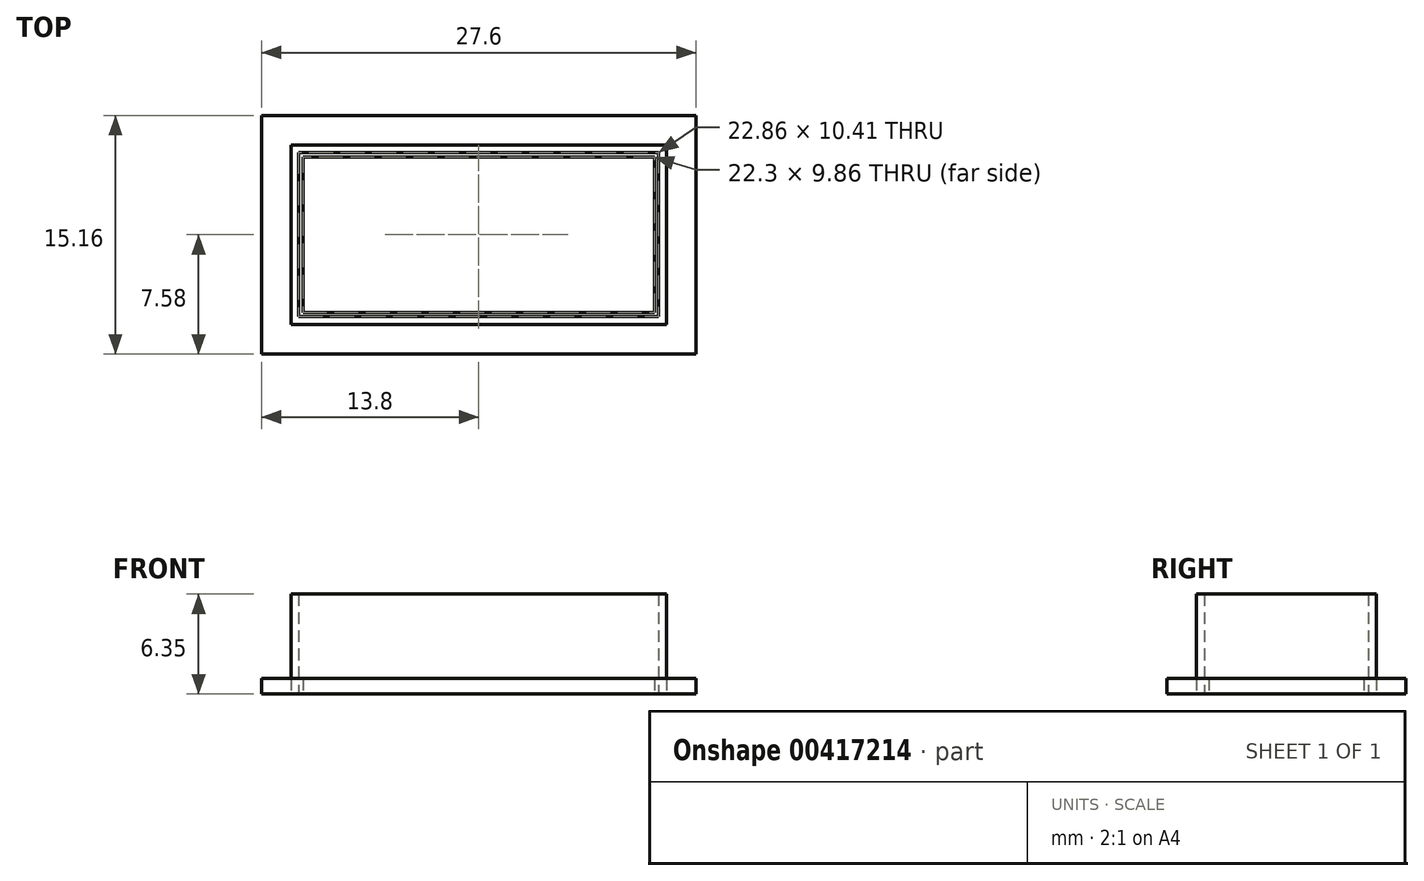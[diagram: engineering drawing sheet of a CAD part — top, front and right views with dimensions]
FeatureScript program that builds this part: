
annotation { "Feature Type Name" : "Feature", "Feature Type Description" : "" }
export const myFeature = defineFeature(function(context is Context, id is Id, definition is map)
    precondition{}
    {
        {
            var Q0;
            Q0=qCreatedBy(makeId("Top.planeOp"),FACE);
            var sketch = newSketch(context, id + "F0", { "sketchPlane" : qUnion([Q0])});
            skLineSegment(sketch, "E0.bottom", {"start": v(-13.8, -7.58) * mm, "end": v(13.8, -7.58) * mm});
            skLineSegment(sketch, "E0.top", {"start": v(-13.8, 7.58) * mm, "end": v(13.8, 7.58) * mm});
            skLineSegment(sketch, "E0.left", {"start": v(-13.8, -7.58) * mm, "end": v(-13.8, 7.58) * mm});
            skLineSegment(sketch, "E0.right", {"start": v(13.8, -7.58) * mm, "end": v(13.8, 7.58) * mm});
            skPoint(sketch, "E0.middle", {"position": v(0, 0) * mm});
            skLineSegment(sketch, "E1.bottom", {"start": v(11.15, 4.93) * mm, "end": v(-11.15, 4.93) * mm});
            skLineSegment(sketch, "E1.top", {"start": v(11.15, -4.93) * mm, "end": v(-11.15, -4.93) * mm});
            skLineSegment(sketch, "E1.left", {"start": v(11.15, 4.93) * mm, "end": v(11.15, -4.93) * mm});
            skLineSegment(sketch, "E1.right", {"start": v(-11.15, 4.93) * mm, "end": v(-11.15, -4.93) * mm});
            skSolve(sketch);
        }
        {
            var Q0;
            Q0=makeQuery(id+"F0.imprint","IMPRINT",FACE,{"disambiguationData":[TD([[makeQuery(id+"F0.imprint","IMPRINT",EDGE,{"derivedFrom":sQuery(id+"F0.wireOp",EDGE,"E0.bottom")}),1.0]])]});
            extrude(context, id + "F1", {"entities" : qUnion([Q0]), "depth" : 1 * mm});
        }
        {
            var Q0;
            Q0=qCreatedBy(makeId("Top.planeOp"),FACE);
            var sketch = newSketch(context, id + "F2", { "sketchPlane" : qUnion([Q0])});
            skLineSegment(sketch, "E2.bottom", {"start": v(11.43, -5.2) * mm, "end": v(-11.43, -5.2) * mm});
            skLineSegment(sketch, "E2.top", {"start": v(11.43, 5.2) * mm, "end": v(-11.43, 5.2) * mm});
            skLineSegment(sketch, "E2.left", {"start": v(11.43, -5.2) * mm, "end": v(11.43, 5.2) * mm});
            skLineSegment(sketch, "E2.right", {"start": v(-11.43, -5.2) * mm, "end": v(-11.43, 5.2) * mm});
            skPoint(sketch, "E2.middle", {"position": v(0, 0) * mm});
            skLineSegment(sketch, "E3.bottom", {"start": v(11.93, -5.7) * mm, "end": v(-11.93, -5.7) * mm});
            skLineSegment(sketch, "E3.top", {"start": v(11.93, 5.7) * mm, "end": v(-11.93, 5.7) * mm});
            skLineSegment(sketch, "E3.left", {"start": v(11.93, -5.7) * mm, "end": v(11.93, 5.7) * mm});
            skLineSegment(sketch, "E3.right", {"start": v(-11.93, -5.7) * mm, "end": v(-11.93, 5.7) * mm});
            skSolve(sketch);
        }
        {
            var Q0;
            Q0=makeQuery(id+"F2.imprint","IMPRINT",FACE,{"disambiguationData":[TD([[makeQuery(id+"F2.imprint","IMPRINT",EDGE,{"derivedFrom":sQuery(id+"F2.wireOp",EDGE,"E2.bottom")}),1.0]])]});
            extrude(context, id + "F3", {"entities" : qUnion([Q0]), "depth" : 6.35 * mm});
        }
    });
